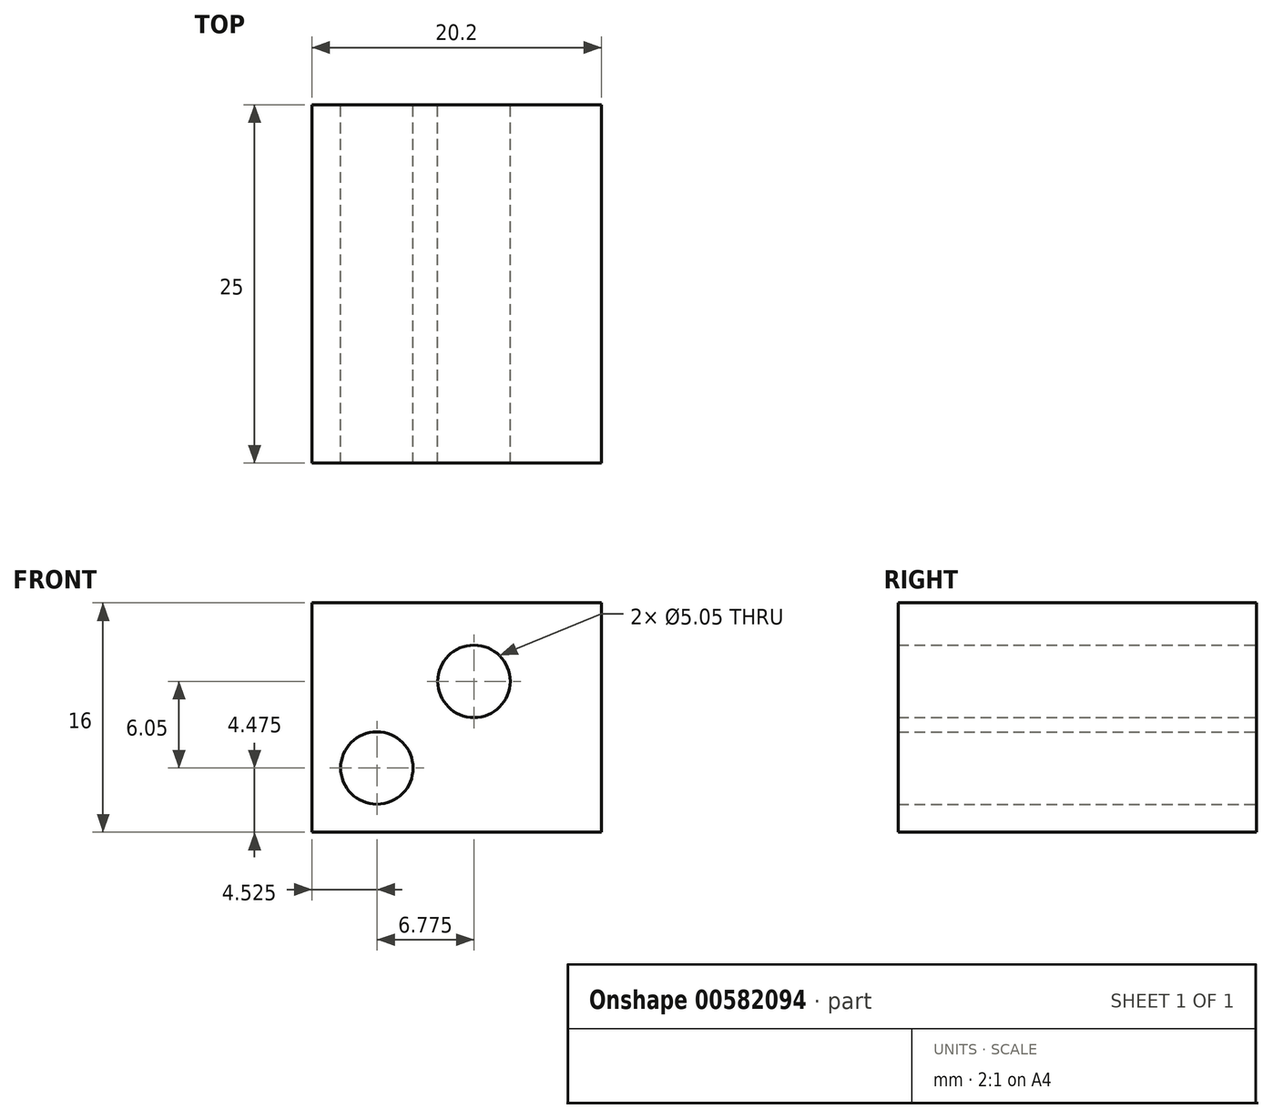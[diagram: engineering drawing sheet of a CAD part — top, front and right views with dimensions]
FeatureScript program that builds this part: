
annotation { "Feature Type Name" : "Feature", "Feature Type Description" : "" }
export const myFeature = defineFeature(function(context is Context, id is Id, definition is map)
    precondition{}
    {
        {
            var Q0;
            Q0=qCreatedBy(makeId("Front.planeOp"),FACE);
            var sketch = newSketch(context, id + "F0", { "sketchPlane" : qUnion([Q0])});
            skLineSegment(sketch, "E0.bottom", {"start": v(10.1, 8) * mm, "end": v(-10.1, 8) * mm});
            skLineSegment(sketch, "E0.top", {"start": v(10.1, -8) * mm, "end": v(-10.1, -8) * mm});
            skLineSegment(sketch, "E0.left", {"start": v(10.1, 8) * mm, "end": v(10.1, -8) * mm});
            skLineSegment(sketch, "E0.right", {"start": v(-10.1, 8) * mm, "end": v(-10.1, -8) * mm});
            skPoint(sketch, "E0.middle", {"position": v(0, 0) * mm});
            skCircle(sketch, "E1", {"center": v(-5.57, -3.53) * mm, "radius": 2.52 * mm});
            skCircle(sketch, "E2", {"center": v(1.2, 2.53) * mm, "radius": 2.52 * mm});
            skPoint(sketch, "E3", {"position": v(-8.1, -3.53) * mm});
            skPoint(sketch, "E4", {"position": v(-5.57, -6.05) * mm});
            skPoint(sketch, "E5", {"position": v(1.2, 0) * mm});
            skSolve(sketch);
        }
        {
            var Q0;
            Q0 = qSketchRegion(id + "F0", true);
            extrude(context, id + "F1", {"entities" : qUnion([Q0]), "depth" : 25 * mm, "offsetDistance" : 25 * mm});
        }
    });
